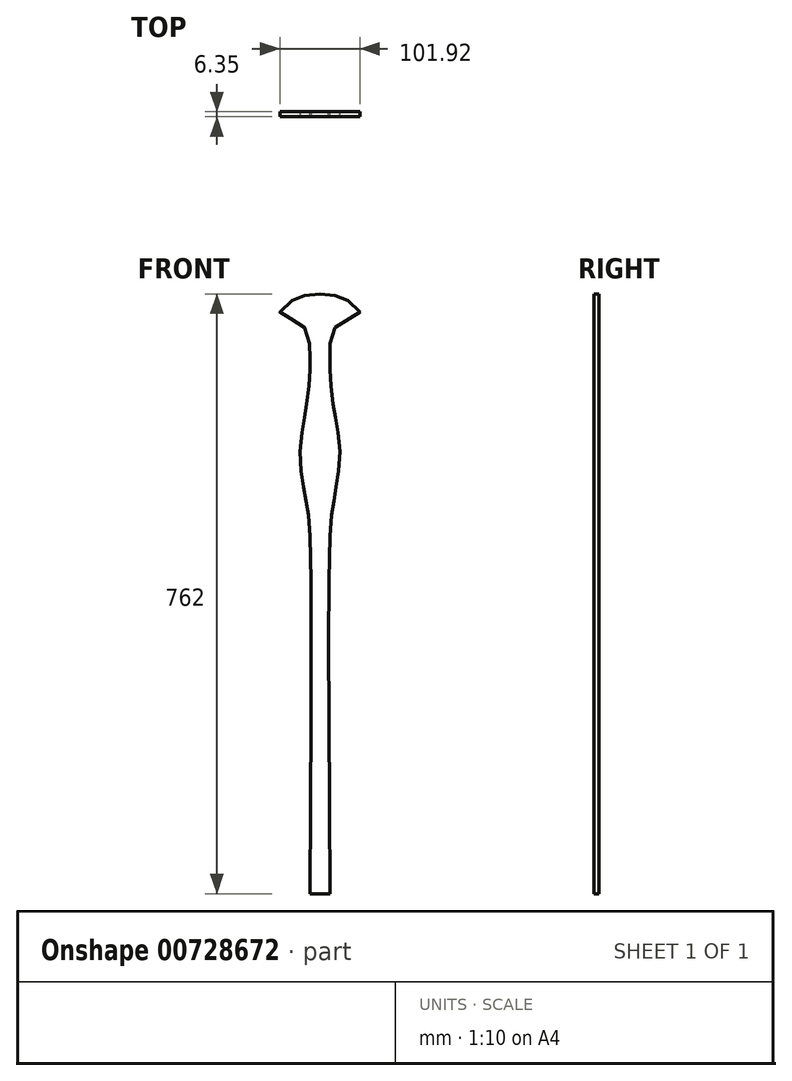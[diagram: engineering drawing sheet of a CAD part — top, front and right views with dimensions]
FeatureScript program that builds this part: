
annotation { "Feature Type Name" : "Feature", "Feature Type Description" : "" }
export const myFeature = defineFeature(function(context is Context, id is Id, definition is map)
    precondition{}
    {
        {
            var Q0;
            Q0=qCreatedBy(makeId("Front.planeOp"),FACE);
            var sketch = newSketch(context, id + "F0", { "sketchPlane" : qUnion([Q0])});
            skPoint(sketch, "E0", {"position": v(12.7, 0) * mm});
            skPoint(sketch, "E1", {"position": v(12.7, 457.2) * mm});
            skPoint(sketch, "E2", {"position": v(19.05, 508) * mm});
            skPoint(sketch, "E3", {"position": v(15.88, 488.95) * mm});
            skPoint(sketch, "E4", {"position": v(22.23, 527.05) * mm});
            skPoint(sketch, "E5", {"position": v(19.05, 609.6) * mm});
            skPoint(sketch, "E6", {"position": v(15.88, 628.65) * mm});
            skPoint(sketch, "E7", {"position": v(22.23, 590.55) * mm});
            skPoint(sketch, "E8", {"position": v(25.4, 558.8) * mm});
            skPoint(sketch, "E9", {"position": v(12.7, 660.4) * mm});
            skPoint(sketch, "E10", {"position": v(12.7, 685.8) * mm});
            skPoint(sketch, "E11", {"position": v(15.24, 711.2) * mm});
            skPoint(sketch, "E12", {"position": v(31.75, 728.98) * mm});
            skPoint(sketch, "E13", {"position": v(50.8, 736.6) * mm});
            skPoint(sketch, "E14", {"position": v(38.1, 751.84) * mm});
            skPoint(sketch, "E15", {"position": v(20.32, 759.46) * mm});
            skPoint(sketch, "E16", {"position": v(0, 762) * mm});
            skPoint(sketch, "E17", {"position": v(12.7, 673.1) * mm});
            skFitSpline(sketch, "E18", {"points": [v(12.7, 0) * mm, v(12.7, 457.2) * mm, v(15.88, 488.95) * mm, v(19.05, 508) * mm, v(22.23, 527.05) * mm, v(25.4, 558.8) * mm, v(22.23, 590.55) * mm, v(19.05, 609.6) * mm, v(15.88, 628.65) * mm, v(12.7, 660.4) * mm, v(12.7, 673.1) * mm, v(12.7, 685.8) * mm, v(15.24, 711.2) * mm, v(31.75, 728.98) * mm, v(50.8, 736.6) * mm, v(38.1, 751.84) * mm, v(20.32, 759.46) * mm, v(0, 762) * mm], "startDerivative": vector(-15.18, 2594.17) * mm, "endDerivative": vector(-867.95, 0) * mm});
            skFitSpline(sketch, "E19.MirrorCS", {"points": [v(-12.7, 0) * mm, v(-12.7, 457.2) * mm, v(-15.88, 488.95) * mm, v(-19.05, 508) * mm, v(-22.23, 527.05) * mm, v(-25.4, 558.8) * mm, v(-22.23, 590.55) * mm, v(-19.05, 609.6) * mm, v(-15.88, 628.65) * mm, v(-12.7, 660.4) * mm, v(-12.7, 673.1) * mm, v(-12.7, 685.8) * mm, v(-15.24, 711.2) * mm, v(-31.75, 728.98) * mm, v(-50.8, 736.6) * mm, v(-38.1, 751.84) * mm, v(-20.32, 759.46) * mm, v(0, 762) * mm], "startDerivative": vector(15.18, 2594.17) * mm, "endDerivative": vector(867.95, 0) * mm});
            skLineSegment(sketch, "E20", {"start": v(-12.7, 0) * mm, "end": v(12.7, 0) * mm});
            skSolve(sketch);
        }
        {
            var Q0;
            Q0=makeQuery(id+"F0.imprint","IMPRINT",FACE,{"disambiguationData":[TD([[makeQuery(id+"F0.imprint","IMPRINT",EDGE,{"derivedFrom":sQuery(id+"F0.wireOp",EDGE,"E18")}),1.0]])]});
            extrude(context, id + "F1", {"entities" : qUnion([Q0]), "depth" : 6.35 * mm, "offsetDistance" : 25.4 * mm});
        }
    });
